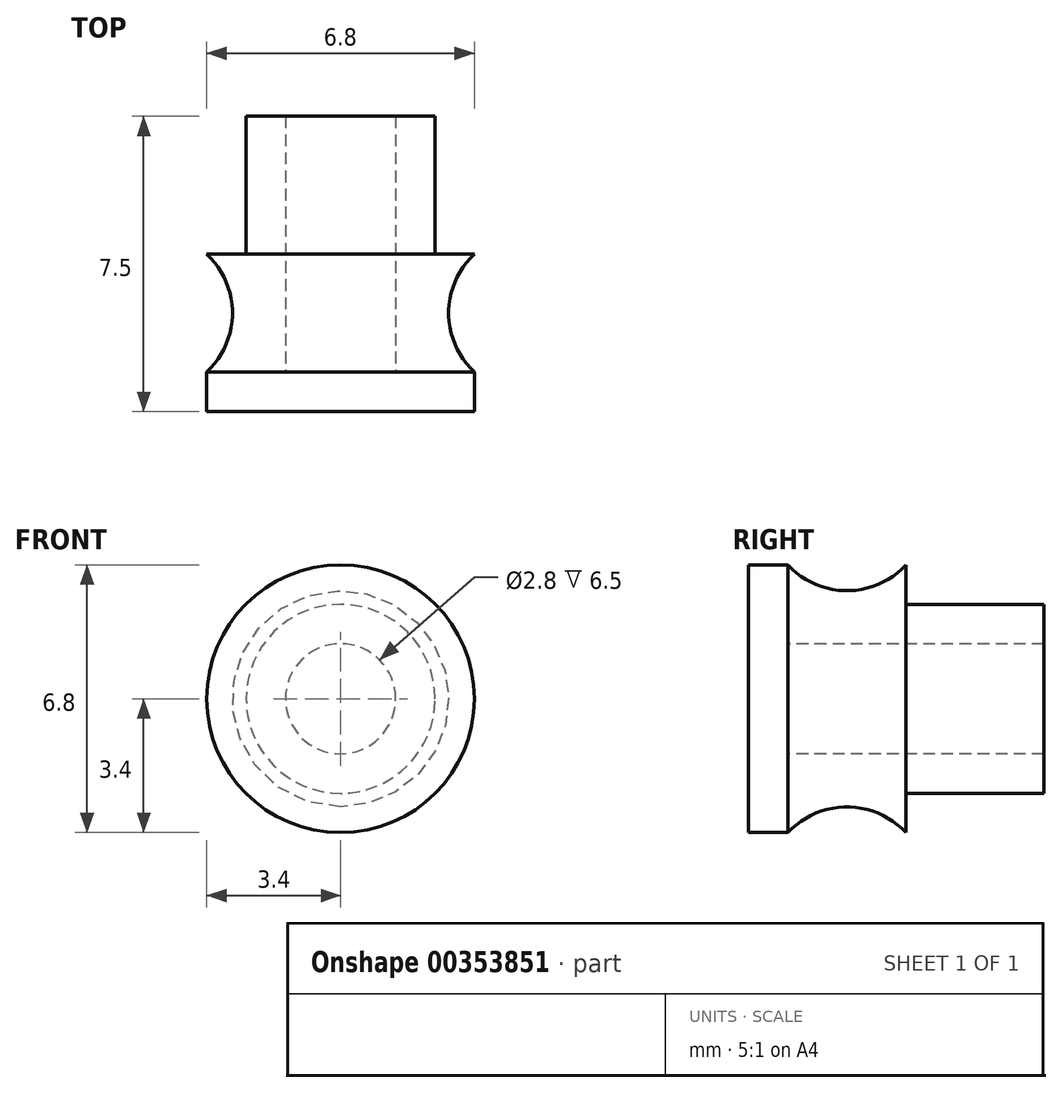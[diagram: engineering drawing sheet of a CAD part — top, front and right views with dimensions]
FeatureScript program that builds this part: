
annotation { "Feature Type Name" : "Feature", "Feature Type Description" : "" }
export const myFeature = defineFeature(function(context is Context, id is Id, definition is map)
    precondition{}
    {
        {
            var Q0;
            Q0=qCreatedBy(makeId("Top.planeOp"),FACE);
            var sketch = newSketch(context, id + "F0", { "sketchPlane" : qUnion([Q0])});
            skLineSegment(sketch, "E0.bottom", {"start": v(1.4, 0) * mm, "end": v(2.4, 0) * mm});
            skLineSegment(sketch, "E0.top", {"start": v(1.4, 6.5) * mm, "end": v(2.4, 6.5) * mm});
            skLineSegment(sketch, "E0.left", {"start": v(1.4, 0) * mm, "end": v(1.4, 6.5) * mm});
            skLineSegment(sketch, "E0.right", {"start": v(2.4, 0) * mm, "end": v(2.4, 6.5) * mm});
            skLineSegment(sketch, "E1.bottom", {"start": v(2.4, 0) * mm, "end": v(2.43, 0) * mm});
            skLineSegment(sketch, "E1.top", {"start": v(2.4, 3) * mm, "end": v(3.4, 3) * mm});
            skLineSegment(sketch, "E1.left", {"start": v(2.4, 0) * mm, "end": v(2.4, 3) * mm});
            skLineSegment(sketch, "E2", {"start": v(0, -1) * mm, "end": v(0, 16.18) * mm, "construction": true});
            skLineSegment(sketch, "E3.bottom", {"start": v(0, 0) * mm, "end": v(3.4, 0) * mm});
            skLineSegment(sketch, "E3.top", {"start": v(0, -1) * mm, "end": v(3.4, -1) * mm});
            skLineSegment(sketch, "E3.left", {"start": v(0, 0) * mm, "end": v(0, -1) * mm});
            skLineSegment(sketch, "E3.right", {"start": v(3.4, 0) * mm, "end": v(3.4, -1) * mm});
            skArc(sketch, "E4", {"start": v(3.4, 3) * mm, "mid": v(2.75, 1.5) * mm, "end": v(3.4, 0) * mm});
            skSolve(sketch);
        }
        {
            var Q0;
            Q0 = qSketchRegion(id + "F0", true);
            var Q1;
            Q1=sQuery(id+"F0.wireOp",EDGE,"E2");
            revolve(context, id + "F1", {"entities" : qUnion([Q0]), "axis" : qUnion([Q1]), "revolveType" : RevolveType.FULL});
        }
    });
